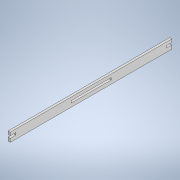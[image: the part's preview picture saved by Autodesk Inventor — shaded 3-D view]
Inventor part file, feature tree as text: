
AUTODESK INVENTOR PART (.ipt)
format: ipt  version: 2022 (Build 260153000, 153)  size: 137,728 bytes
history: native  units: in
note: dims shown in document units (in); Inventor stores cm internally (conversion verified against a paired STEP export)
features: extrude x4, sketch x4
ambient origin geometry x8: Origin, YZ Plane, XZ Plane, XY Plane, X Axis, Y Axis, Z Axis, Center Point
bodies: Solid1 (feature_tree)
feature tree (8):
  extrude  "Extrusion1"  Depth=1.439in
  extrude  "Extrusion2"  Depth=0.0197in
  extrude  "Extrusion3"  Depth=0.0492in TaperAngle=0.0deg
  extrude  "Extrusion4"  TaperAngle=45.0deg  [1 undecoded]
  sketch  "Sketch1"  dims[d0=0.0787in d1=1.439in]
  sketch  "Sketch2"  dims[d2=0.0197in d3=0.0in d4=0.0197in]
  sketch  "Sketch3"  dims[d6=0.0492in d7=0.0236in d8=0.0in]
  sketch  "Sketch4"  dims[d9=0.0276in d10=45.0deg d11=45.0deg d12=0.0591in d13=0.0236in d14=0.0in d15=0.0197in d16=0.0197in d17=0.3563in d18=0.1781in d19=0.0276in d20=0.3937in d21=0.0in]
note: 1 required parameter value undecoded (feature->parameter linkage not recoverable at this tier; creation-order binding heuristic only, values carry confidence <= 0.55)
